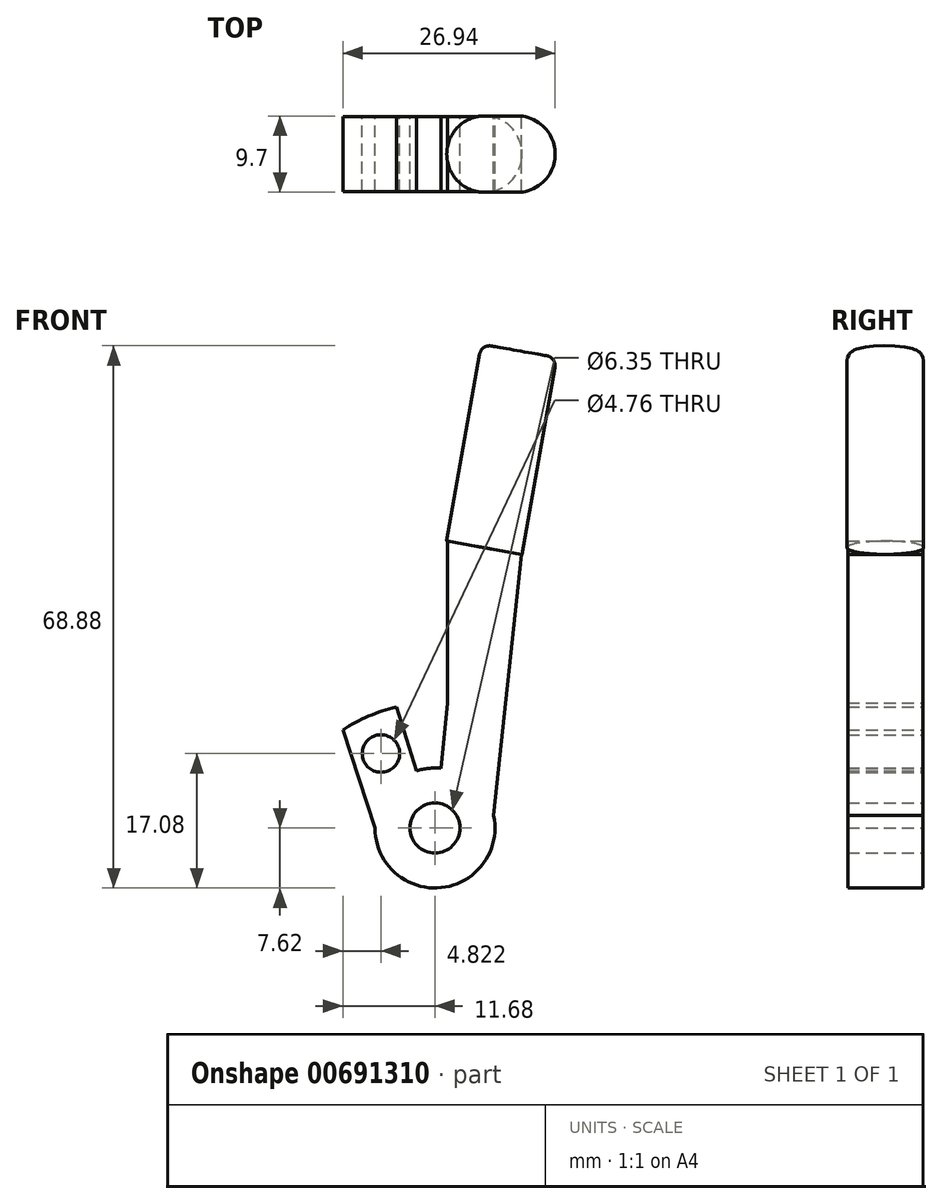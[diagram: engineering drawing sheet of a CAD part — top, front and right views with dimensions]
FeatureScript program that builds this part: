
annotation { "Feature Type Name" : "Feature", "Feature Type Description" : "" }
export const myFeature = defineFeature(function(context is Context, id is Id, definition is map)
    precondition{}
    {
        {
            var Q0;
            Q0=qCreatedBy(makeId("Front.planeOp"),FACE);
            var sketch = newSketch(context, id + "F0", { "sketchPlane" : qUnion([Q0])});
            skCircle(sketch, "E0", {"center": v(0, 0) * mm, "radius": 3.18 * mm});
            skCircle(sketch, "E1", {"center": v(0, 0) * mm, "radius": 7.62 * mm});
            skLineSegment(sketch, "E2", {"start": v(1.59, 56.2) * mm, "end": v(1.59, 13.66) * mm, "construction": true});
            skLineSegment(sketch, "E3", {"start": v(-1.59, 56.2) * mm, "end": v(-1.59, 12.68) * mm, "construction": true});
            skLineSegment(sketch, "E4.bottom", {"start": v(-15.01, 15.87) * mm, "end": v(27.66, 15.87) * mm, "construction": true});
            skLineSegment(sketch, "E4.top", {"start": v(-15.01, 0) * mm, "end": v(27.66, 0) * mm, "construction": true});
            skLineSegment(sketch, "E4.left", {"start": v(-15.01, 15.87) * mm, "end": v(-15.01, 0) * mm, "construction": true});
            skLineSegment(sketch, "E4.right", {"start": v(27.66, 15.87) * mm, "end": v(27.66, 0) * mm, "construction": true});
            skLineSegment(sketch, "E5", {"start": v(0, 0) * mm, "end": v(10.45, 59.25) * mm, "construction": true});
            skLineSegment(sketch, "E6", {"start": v(5.61, 59.25) * mm, "end": v(1.59, 36.43) * mm, "construction": true});
            skLineSegment(sketch, "E7", {"start": v(10.1, 57.3) * mm, "end": v(14.8, 56.46) * mm, "construction": true});
            skLineSegment(sketch, "E8", {"start": v(14.8, 56.46) * mm, "end": v(5.72, 5.03) * mm, "construction": true});
            skLineSegment(sketch, "E9", {"start": v(0, 0) * mm, "end": v(43.05, 9.15) * mm, "construction": true});
            skLineSegment(sketch, "E10", {"start": v(1.59, 36.43) * mm, "end": v(10.97, 34.78) * mm});
            skLineSegment(sketch, "E11", {"start": v(10.97, 34.78) * mm, "end": v(7.45, 1.58) * mm});
            skLineSegment(sketch, "E12", {"start": v(1.59, 15.87) * mm, "end": v(0, 0) * mm});
            skLineSegment(sketch, "E13", {"start": v(-1.59, 15.87) * mm, "end": v(0, 0) * mm});
            skLineSegment(sketch, "E14", {"start": v(1.59, 36.43) * mm, "end": v(1.59, 15.87) * mm});
            skCircle(sketch, "E15", {"center": v(0, 0) * mm, "radius": 18.26 * mm, "construction": true});
            skLineSegment(sketch, "E16", {"start": v(0, 0) * mm, "end": v(8.97, 15.9) * mm, "construction": true});
            skLineSegment(sketch, "E17", {"start": v(0, 0) * mm, "end": v(12.08, 13.69) * mm, "construction": true});
            skLineSegment(sketch, "E18", {"start": v(7.62, 0) * mm, "end": v(12.08, 13.69) * mm, "construction": true});
            skLineSegment(sketch, "E19", {"start": v(0, 0) * mm, "end": v(-45.49, 8.02) * mm, "construction": true});
            skLineSegment(sketch, "E20.MirrorCS", {"start": v(0, 0) * mm, "end": v(-12.08, 13.69) * mm, "construction": true});
            skLineSegment(sketch, "E21", {"start": v(-12.08, 13.69) * mm, "end": v(-7.62, 0) * mm});
            skLineSegment(sketch, "E22", {"start": v(0, 0) * mm, "end": v(0, -5.46) * mm});
            skArc(sketch, "E23", {"start": v(-1.59, 15.87) * mm, "mid": v(-6.85, 14.8) * mm, "end": v(-11.68, 12.46) * mm});
            skLineSegment(sketch, "E24", {"start": v(0, 0) * mm, "end": v(-4.9, 15.36) * mm});
            skCircle(sketch, "E25", {"center": v(0, 0) * mm, "radius": 4.76 * mm, "construction": true});
            skLineSegment(sketch, "E26", {"start": v(-10.33, 8.33) * mm, "end": v(-3.38, 10.6) * mm, "construction": true});
            skCircle(sketch, "E27", {"center": v(-6.86, 9.46) * mm, "radius": 2.38 * mm});
            skLineSegment(sketch, "E28", {"start": v(-6.86, 9.46) * mm, "end": v(-6.86, 0) * mm, "construction": true});
            skCircle(sketch, "E29", {"center": v(-6.86, 9.46) * mm, "radius": 3.96 * mm, "construction": true});
            skLineSegment(sketch, "E30", {"start": v(0, 0) * mm, "end": v(-6.86, 9.46) * mm, "construction": true});
            skSolve(sketch);
        }
        {
            var Q0;
            Q0=makeQuery(id+"F0.imprint","IMPRINT",FACE,{"disambiguationData":[TD([[makeQuery(id+"F0.imprint","IMPRINT",EDGE,{"derivedFrom":sQuery(id+"F0.wireOp",EDGE,"E10")}),-1.0]])]});
            var Q1;
            {var subQ0=sQuery(id+"F0.wireOp",EDGE,"E12");var subQ3=sQuery(id+"F0.wireOp",EDGE,"E0");var subQ4=makeQuery(id+"F0.imprint","INTERSECT",VERTEX,{"derivedFrom":[subQ3,subQ0]});Q1=makeQuery(id+"F0.imprint","IMPRINT",FACE,{"disambiguationData":[TD([[makeQuery(id+"F0.imprint","IMPRINT",EDGE,{"disambiguationData":[TD([[subQ4,1.0]])],"derivedFrom":subQ3}),-1.0]])]});}
            var Q2;
            {var subQ0=sQuery(id+"F0.wireOp",EDGE,"E12");var subQ1=sQuery(id+"F0.wireOp",EDGE,"E0");var subQ2=makeQuery(id+"F0.imprint","INTERSECT",VERTEX,{"derivedFrom":[subQ1,subQ0]});Q2=makeQuery(id+"F0.imprint","IMPRINT",FACE,{"disambiguationData":[TD([[makeQuery(id+"F0.imprint","IMPRINT",EDGE,{"disambiguationData":[TD([[subQ2,-1.0]])],"derivedFrom":subQ1}),-1.0]])]});}
            var Q3;
            {var subQ0=sQuery(id+"F0.wireOp",EDGE,"E13");var subQ1=sQuery(id+"F0.wireOp",EDGE,"E0");var subQ2=makeQuery(id+"F0.imprint","INTERSECT",VERTEX,{"derivedFrom":[subQ1,subQ0]});Q3=makeQuery(id+"F0.imprint","IMPRINT",FACE,{"disambiguationData":[TD([[makeQuery(id+"F0.imprint","IMPRINT",EDGE,{"disambiguationData":[TD([[subQ2,-1.0]])],"derivedFrom":subQ1}),-1.0]])]});}
            var Q4;
            {var subQ0=sQuery(id+"F0.wireOp",EDGE,"E21");var subQ1=sQuery(id+"F0.wireOp",EDGE,"E1");var subQ2=makeQuery(id+"F0.imprint","INTERSECT",VERTEX,{"derivedFrom":[subQ1,subQ0]});Q4=makeQuery(id+"F0.imprint","IMPRINT",FACE,{"disambiguationData":[TD([[makeQuery(id+"F0.imprint","IMPRINT",EDGE,{"disambiguationData":[TD([[subQ2,1.0]])],"derivedFrom":subQ1}),-1.0]])]});}
            extrude(context, id + "F1", {"entities" : qUnion([Q0, Q1, Q2, Q3, Q4]), "depth" : 9.52 * mm, "offsetDistance" : 25.4 * mm});
        }
        {
            var Q0;
            Q0=makeQuery(id+"F1.opExtrude","SWEPT_FACE",FACE,{"disambiguationData":[OSD([sQuery(id+"F0.wireOp",EDGE,"E10")])]});
            var Q1;
            Q1=makeQuery(id+"F1.opExtrude","SWEPT_FACE",FACE,{"disambiguationData":[OSD([sQuery(id+"F0.wireOp",EDGE,"E10")])]});
            var Q2;
            Q2=makeQuery(id+"F1.opExtrude","SWEPT_FACE",FACE,{"disambiguationData":[OSD([sQuery(id+"F0.wireOp",EDGE,"E10")])]});
            var Q3;
            Q3=makeQuery(id+"F1.opExtrude","SWEPT_FACE",FACE,{"disambiguationData":[OSD([sQuery(id+"F0.wireOp",EDGE,"E10")])]});
            var sketch = newSketch(context, id + "F2", { "sketchPlane" : qUnion([Q0, Q1, Q2, Q3])});
            skLineSegment(sketch, "E31", {"start": v(0, 2.44) * mm, "end": v(0, 21.59) * mm, "construction": true});
            skLineSegment(sketch, "E32", {"start": v(0, 21.59) * mm, "end": v(0, -14.09) * mm, "construction": true});
            skPoint(sketch, "E32.endSnap0", {"position": v(0, -9.53) * mm});
            skLineSegment(sketch, "E33", {"start": v(0, -14.09) * mm, "end": v(0, -30.3) * mm, "construction": true});
            skLineSegment(sketch, "E34", {"start": v(4.76, -4.76) * mm, "end": v(-27.5, -4.76) * mm, "construction": true});
            skPoint(sketch, "E34.endSnap0", {"position": v(-4.76, -4.76) * mm});
            skCircle(sketch, "E35", {"center": v(0, -4.76) * mm, "radius": 4.85 * mm});
            skSolve(sketch);
        }
        {
            var Q0;
            Q0 = qSketchRegion(id + "F2", true);
            extrude(context, id + "F3", {"entities" : qUnion([Q0]), "operationType" : NewBodyOperationType.ADD, "depth" : 25.4 * mm, "offsetDistance" : 25.4 * mm});
        }
        {
            var Q0;
            Q0=makeQuery(id+"F3.opExtrude","CAP_EDGE",EDGE,{"disambiguationData":[OSD([sQuery(id+"F2.wireOp",EDGE,"E35")])],"isStart":false});
            fillet(context, id + "F4", {"entities" : qUnion([Q0]), "radius" : 1.27 * mm, "tangentPropagation" : true, "allowEdgeOverflow" : false});
        }
        {
            var Q0;
            Q0=makeQuery(id+"F0.imprint","IMPRINT",FACE,{"disambiguationData":[TD([[makeQuery(id+"F0.imprint","IMPRINT",EDGE,{"derivedFrom":sQuery(id+"F0.wireOp",EDGE,"E27")}),1.0]])]});
            extrude(context, id + "F5", {"entities" : qUnion([Q0]), "operationType" : NewBodyOperationType.REMOVE, "oppositeDirection" : true, "depth" : 9.65 * mm, "offsetDistance" : 25.4 * mm});
        }
    });
